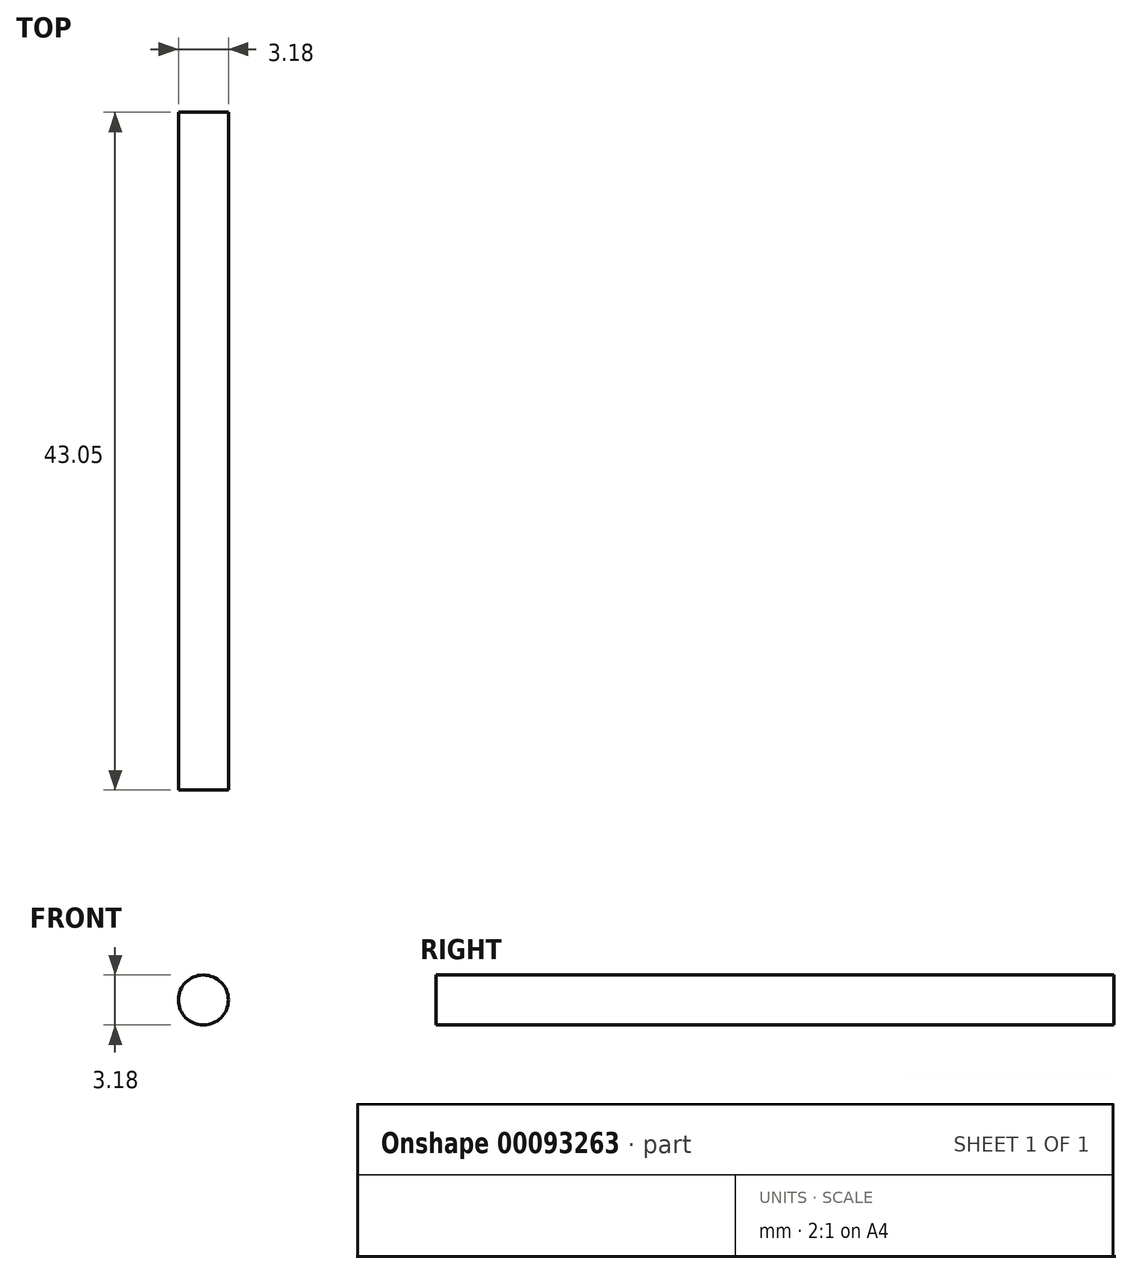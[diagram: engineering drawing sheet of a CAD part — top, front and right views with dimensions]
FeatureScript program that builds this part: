
annotation { "Feature Type Name" : "Feature", "Feature Type Description" : "" }
export const myFeature = defineFeature(function(context is Context, id is Id, definition is map)
    precondition{}
    {
        {
            var Q0;
            Q0=qCreatedBy(makeId("Front.planeOp"),FACE);
            var sketch = newSketch(context, id + "F0", { "sketchPlane" : qUnion([Q0])});
            skCircle(sketch, "E0", {"center": v(0, 0) * mm, "radius": 1.59 * mm});
            skSolve(sketch);
        }
        {
            var Q0;
            Q0=qSketchRegion(id+"F0",true);
            extrude(context, id + "F1", {"entities" : qUnion([Q0]), "depth" : 43.05 * mm});
        }
    });
